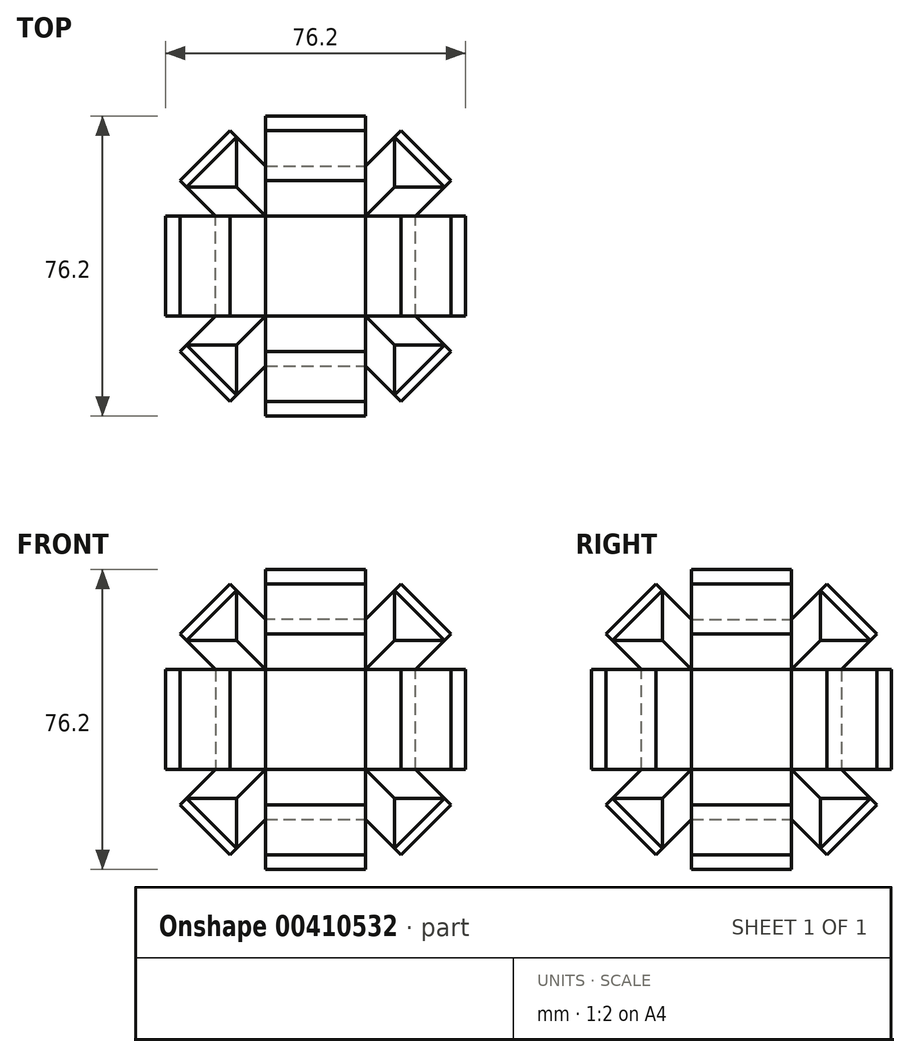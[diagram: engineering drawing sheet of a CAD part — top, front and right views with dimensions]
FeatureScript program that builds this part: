
annotation { "Feature Type Name" : "Feature", "Feature Type Description" : "" }
export const myFeature = defineFeature(function(context is Context, id is Id, definition is map)
    precondition{}
    {
        {
            var Q0;
            Q0=qCreatedBy(makeId("Front.planeOp"),FACE);
            var sketch = newSketch(context, id + "F0", { "sketchPlane" : qUnion([Q0])});
            skLineSegment(sketch, "E0.bottom", {"start": v(-25.4, -25.4) * mm, "end": v(25.4, -25.4) * mm});
            skLineSegment(sketch, "E0.top", {"start": v(-25.4, 25.4) * mm, "end": v(25.4, 25.4) * mm});
            skLineSegment(sketch, "E0.left", {"start": v(-25.4, -25.4) * mm, "end": v(-25.4, 25.4) * mm});
            skLineSegment(sketch, "E0.right", {"start": v(25.4, -25.4) * mm, "end": v(25.4, 25.4) * mm});
            skPoint(sketch, "E0.middle", {"position": v(0, 0) * mm});
            skSolve(sketch);
        }
        {
            var Q0;
            Q0 = qSketchRegion(id + "F0", true);
            extrude(context, id + "F1", {"entities" : qUnion([Q0]), "depth" : 25.4 * mm, "hasSecondDirection" : true, "secondDirectionOppositeDirection" : true, "secondDirectionDepth" : 25.4 * mm});
        }
        {
            var Q0;
            Q0=makeQuery(id+"F1.opExtrude","SWEPT_FACE",FACE,{"disambiguationData":[OSD([sQuery(id+"F0.wireOp",EDGE,"E0.left")])]});
            var Q1;
            Q1=makeQuery(id+"F1.opExtrude","SWEPT_FACE",FACE,{"disambiguationData":[OSD([sQuery(id+"F0.wireOp",EDGE,"E0.bottom")])]});
            var Q2;
            Q2=makeQuery(id+"F1.opExtrude","CAP_FACE",FACE,{"disambiguationData":[OSD([sQuery(id+"F0.wireOp",EDGE,"E0.bottom"),sQuery(id+"F0.wireOp",EDGE,"E0.top"),sQuery(id+"F0.wireOp",EDGE,"E0.left"),sQuery(id+"F0.wireOp",EDGE,"E0.right")])],"isStart":true});
            var Q3;
            Q3=makeQuery(id+"F1.opExtrude","SWEPT_FACE",FACE,{"disambiguationData":[OSD([sQuery(id+"F0.wireOp",EDGE,"E0.right")])]});
            var Q4;
            Q4=makeQuery(id+"F1.opExtrude","SWEPT_FACE",FACE,{"disambiguationData":[OSD([sQuery(id+"F0.wireOp",EDGE,"E0.top")])]});
            var Q5;
            Q5=makeQuery(id+"F1.opExtrude","CAP_FACE",FACE,{"disambiguationData":[OSD([sQuery(id+"F0.wireOp",EDGE,"E0.bottom"),sQuery(id+"F0.wireOp",EDGE,"E0.top"),sQuery(id+"F0.wireOp",EDGE,"E0.left"),sQuery(id+"F0.wireOp",EDGE,"E0.right")])],"isStart":false});
            chamfer(context, id + "F2", {"entities" : qUnion([Q0, Q1, Q2, Q3, Q4, Q5]), "width" : 12.7 * mm, "tangentPropagation" : true});
        }
        {
            var Q0;
            Q0=makeQuery(id+"F1.opExtrude","SWEPT_FACE",FACE,{"disambiguationData":[OSD([sQuery(id+"F0.wireOp",EDGE,"E0.top")])]});
            extrude(context, id + "F3", {"entities" : qUnion([Q0]), "operationType" : NewBodyOperationType.ADD, "depth" : 12.7 * mm});
        }
        {
            var Q0;
            Q0=makeQuery(id+"F1.opExtrude","SWEPT_FACE",FACE,{"disambiguationData":[OSD([sQuery(id+"F0.wireOp",EDGE,"E0.left")])]});
            extrude(context, id + "F4", {"entities" : qUnion([Q0]), "operationType" : NewBodyOperationType.ADD, "depth" : 12.7 * mm});
        }
        {
            var Q0;
            Q0=makeQuery(id+"F1.opExtrude","CAP_FACE",FACE,{"disambiguationData":[OSD([sQuery(id+"F0.wireOp",EDGE,"E0.bottom"),sQuery(id+"F0.wireOp",EDGE,"E0.top"),sQuery(id+"F0.wireOp",EDGE,"E0.left"),sQuery(id+"F0.wireOp",EDGE,"E0.right")])],"isStart":true});
            extrude(context, id + "F5", {"entities" : qUnion([Q0]), "operationType" : NewBodyOperationType.ADD, "depth" : 12.7 * mm});
        }
        {
            var Q0;
            Q0=makeQuery(id+"F1.opExtrude","SWEPT_FACE",FACE,{"disambiguationData":[OSD([sQuery(id+"F0.wireOp",EDGE,"E0.bottom")])]});
            extrude(context, id + "F6", {"entities" : qUnion([Q0]), "operationType" : NewBodyOperationType.ADD, "depth" : 12.7 * mm});
        }
        {
            var Q0;
            Q0=makeQuery(id+"F1.opExtrude","SWEPT_FACE",FACE,{"disambiguationData":[OSD([sQuery(id+"F0.wireOp",EDGE,"E0.right")])]});
            extrude(context, id + "F7", {"entities" : qUnion([Q0]), "operationType" : NewBodyOperationType.ADD, "depth" : 12.7 * mm});
        }
        {
            var Q0;
            Q0=makeQuery(id+"F1.opExtrude","CAP_FACE",FACE,{"disambiguationData":[OSD([sQuery(id+"F0.wireOp",EDGE,"E0.bottom"),sQuery(id+"F0.wireOp",EDGE,"E0.top"),sQuery(id+"F0.wireOp",EDGE,"E0.left"),sQuery(id+"F0.wireOp",EDGE,"E0.right")])],"isStart":false});
            extrude(context, id + "F8", {"entities" : qUnion([Q0]), "operationType" : NewBodyOperationType.ADD, "depth" : 12.7 * mm});
        }
        {
            var Q0;
            {var subQ0=sQuery(id+"F0.wireOp",EDGE,"E0.top");Q0=makeQuery(id+"F2.opChamfer","BLEND_FACE",FACE,{"disambiguationData":[OSD([subQ0]),TDD([makeQuery(id+"F1.opExtrude","CAP_EDGE",EDGE,{"disambiguationData":[OSD([subQ0])],"isStart":true})])]});}
            extrude(context, id + "F9", {"entities" : qUnion([Q0]), "operationType" : NewBodyOperationType.ADD, "depth" : 12.7 * mm});
        }
        {
            var Q0;
            {var subQ0=sQuery(id+"F0.wireOp",EDGE,"E0.right");var subQ1=sQuery(id+"F0.wireOp",EDGE,"E0.top");Q0=makeQuery(id+"F2.opChamfer","BLEND_FACE",FACE,{"disambiguationData":[OSD([subQ1,subQ0]),TDD([makeQuery(id+"F1.opExtrude","SWEPT_EDGE",EDGE,{"disambiguationData":[OSD([subQ1,subQ0])]})])]});}
            extrude(context, id + "F10", {"entities" : qUnion([Q0]), "operationType" : NewBodyOperationType.ADD, "depth" : 12.7 * mm});
        }
        {
            var Q0;
            {var subQ0=sQuery(id+"F0.wireOp",EDGE,"E0.top");Q0=makeQuery(id+"F2.opChamfer","BLEND_FACE",FACE,{"disambiguationData":[OSD([subQ0]),TDD([makeQuery(id+"F1.opExtrude","CAP_EDGE",EDGE,{"disambiguationData":[OSD([subQ0])],"isStart":false})])]});}
            extrude(context, id + "F11", {"entities" : qUnion([Q0]), "operationType" : NewBodyOperationType.ADD, "depth" : 12.7 * mm});
        }
        {
            var Q0;
            {var subQ0=sQuery(id+"F0.wireOp",EDGE,"E0.left");var subQ1=sQuery(id+"F0.wireOp",EDGE,"E0.top");Q0=makeQuery(id+"F2.opChamfer","BLEND_FACE",FACE,{"disambiguationData":[OSD([subQ1,subQ0]),TDD([makeQuery(id+"F1.opExtrude","SWEPT_EDGE",EDGE,{"disambiguationData":[OSD([subQ1,subQ0])]})])]});}
            extrude(context, id + "F12", {"entities" : qUnion([Q0]), "operationType" : NewBodyOperationType.ADD, "depth" : 12.7 * mm});
        }
        {
            var Q0;
            {var subQ0=sQuery(id+"F0.wireOp",EDGE,"E0.bottom");Q0=makeQuery(id+"F2.opChamfer","BLEND_FACE",FACE,{"disambiguationData":[OSD([subQ0]),TDD([makeQuery(id+"F1.opExtrude","CAP_EDGE",EDGE,{"disambiguationData":[OSD([subQ0])],"isStart":true})])]});}
            extrude(context, id + "F13", {"entities" : qUnion([Q0]), "operationType" : NewBodyOperationType.ADD, "depth" : 12.7 * mm});
        }
        {
            var Q0;
            {var subQ0=sQuery(id+"F0.wireOp",EDGE,"E0.left");var subQ1=sQuery(id+"F0.wireOp",EDGE,"E0.bottom");Q0=makeQuery(id+"F2.opChamfer","BLEND_FACE",FACE,{"disambiguationData":[OSD([subQ1,subQ0]),TDD([makeQuery(id+"F1.opExtrude","SWEPT_EDGE",EDGE,{"disambiguationData":[OSD([subQ1,subQ0])]})])]});}
            extrude(context, id + "F14", {"entities" : qUnion([Q0]), "operationType" : NewBodyOperationType.ADD, "depth" : 12.7 * mm});
        }
        {
            var Q0;
            {var subQ0=sQuery(id+"F0.wireOp",EDGE,"E0.bottom");Q0=makeQuery(id+"F2.opChamfer","BLEND_FACE",FACE,{"disambiguationData":[OSD([subQ0]),TDD([makeQuery(id+"F1.opExtrude","CAP_EDGE",EDGE,{"disambiguationData":[OSD([subQ0])],"isStart":false})])]});}
            extrude(context, id + "F15", {"entities" : qUnion([Q0]), "operationType" : NewBodyOperationType.ADD, "depth" : 12.7 * mm});
        }
        {
            var Q0;
            {var subQ0=sQuery(id+"F0.wireOp",EDGE,"E0.left");Q0=makeQuery(id+"F2.opChamfer","BLEND_FACE",FACE,{"disambiguationData":[OSD([subQ0]),TDD([makeQuery(id+"F1.opExtrude","CAP_EDGE",EDGE,{"disambiguationData":[OSD([subQ0])],"isStart":false})])]});}
            extrude(context, id + "F16", {"entities" : qUnion([Q0]), "operationType" : NewBodyOperationType.ADD, "depth" : 12.7 * mm});
        }
        {
            var Q0;
            {var subQ0=sQuery(id+"F0.wireOp",EDGE,"E0.left");Q0=makeQuery(id+"F2.opChamfer","BLEND_FACE",FACE,{"disambiguationData":[OSD([subQ0]),TDD([makeQuery(id+"F1.opExtrude","CAP_EDGE",EDGE,{"disambiguationData":[OSD([subQ0])],"isStart":true})])]});}
            extrude(context, id + "F17", {"entities" : qUnion([Q0]), "operationType" : NewBodyOperationType.ADD, "depth" : 12.7 * mm});
        }
        {
            var Q0;
            {var subQ0=sQuery(id+"F0.wireOp",EDGE,"E0.right");Q0=makeQuery(id+"F2.opChamfer","BLEND_FACE",FACE,{"disambiguationData":[OSD([subQ0]),TDD([makeQuery(id+"F1.opExtrude","CAP_EDGE",EDGE,{"disambiguationData":[OSD([subQ0])],"isStart":true})])]});}
            extrude(context, id + "F18", {"entities" : qUnion([Q0]), "operationType" : NewBodyOperationType.ADD, "depth" : 12.7 * mm});
        }
        {
            var Q0;
            {var subQ0=sQuery(id+"F0.wireOp",EDGE,"E0.right");Q0=makeQuery(id+"F2.opChamfer","BLEND_FACE",FACE,{"disambiguationData":[OSD([subQ0]),TDD([makeQuery(id+"F1.opExtrude","CAP_EDGE",EDGE,{"disambiguationData":[OSD([subQ0])],"isStart":false})])]});}
            extrude(context, id + "F19", {"entities" : qUnion([Q0]), "operationType" : NewBodyOperationType.ADD, "depth" : 12.7 * mm});
        }
        {
            var Q0;
            {var subQ0=sQuery(id+"F0.wireOp",EDGE,"E0.right");var subQ1=sQuery(id+"F0.wireOp",EDGE,"E0.bottom");Q0=makeQuery(id+"F2.opChamfer","BLEND_FACE",FACE,{"disambiguationData":[OSD([subQ1,subQ0]),TDD([makeQuery(id+"F1.opExtrude","SWEPT_EDGE",EDGE,{"disambiguationData":[OSD([subQ1,subQ0])]})])]});}
            extrude(context, id + "F20", {"entities" : qUnion([Q0]), "operationType" : NewBodyOperationType.ADD, "depth" : 12.7 * mm});
        }
        {
            var Q0;
            {var subQ0=sQuery(id+"F0.wireOp",EDGE,"E0.right");var subQ1=sQuery(id+"F0.wireOp",EDGE,"E0.top");Q0=makeQuery(id+"F2.opChamfer","BLEND_FACE",FACE,{"disambiguationData":[OSD([subQ1,subQ0]),TDD([makeQuery(id+"F1.opExtrude","CAP_VERTEX",VERTEX,{"disambiguationData":[OSD([subQ1,subQ0])],"isStart":false})])]});}
            var sketch = newSketch(context, id + "F21", { "sketchPlane" : qUnion([Q0])});
            skSolve(sketch);
        }
        {
            var Q0;
            {var subQ0=sQuery(id+"F0.wireOp",EDGE,"E0.right");var subQ1=sQuery(id+"F0.wireOp",EDGE,"E0.top");var subQ2=makeQuery(id+"F1.opExtrude","CAP_VERTEX",VERTEX,{"disambiguationData":[OSD([subQ1,subQ0])],"isStart":false});Q0=makeQuery(id+"F21.imprint","IMPRINT",FACE,{"disambiguationData":[TD([[makeQuery(id+"F21.imprint","IMPRINT",EDGE,{"derivedFrom":makeQuery(id+"F11.boolean.opBoolean","MERGE",EDGE,{"derivedFrom":[makeQuery(id+"F2.opChamfer","BLEND_EDGE",EDGE,{"blendedFrom":[subQ2,makeQuery(id+"F1.opExtrude","CAP_EDGE",EDGE,{"disambiguationData":[OSD([subQ1])],"isStart":false})],"blendedInto":[]}),makeQuery(id+"F11.opExtrude","CAP_EDGE",EDGE,{"disambiguationData":[OSD([subQ1,subQ0])],"isStart":true})]})}),-1.0]])]});}
            extrude(context, id + "F22", {"entities" : qUnion([Q0]), "operationType" : NewBodyOperationType.ADD, "depth" : 12.7 * mm});
        }
        {
            var Q0;
            {var subQ0=sQuery(id+"F0.wireOp",EDGE,"E0.right");var subQ1=sQuery(id+"F0.wireOp",EDGE,"E0.top");Q0=makeQuery(id+"F2.opChamfer","BLEND_FACE",FACE,{"disambiguationData":[OSD([subQ1,subQ0]),TDD([makeQuery(id+"F1.opExtrude","CAP_VERTEX",VERTEX,{"disambiguationData":[OSD([subQ1,subQ0])],"isStart":true})])]});}
            extrude(context, id + "F23", {"entities" : qUnion([Q0]), "operationType" : NewBodyOperationType.ADD, "depth" : 12.7 * mm});
        }
        {
            var Q0;
            {var subQ0=sQuery(id+"F0.wireOp",EDGE,"E0.left");var subQ1=sQuery(id+"F0.wireOp",EDGE,"E0.top");Q0=makeQuery(id+"F2.opChamfer","BLEND_FACE",FACE,{"disambiguationData":[OSD([subQ1,subQ0]),TDD([makeQuery(id+"F1.opExtrude","CAP_VERTEX",VERTEX,{"disambiguationData":[OSD([subQ1,subQ0])],"isStart":true})])]});}
            extrude(context, id + "F24", {"entities" : qUnion([Q0]), "operationType" : NewBodyOperationType.ADD, "depth" : 12.7 * mm});
        }
        {
            var Q0;
            {var subQ0=sQuery(id+"F0.wireOp",EDGE,"E0.left");var subQ1=sQuery(id+"F0.wireOp",EDGE,"E0.top");Q0=makeQuery(id+"F2.opChamfer","BLEND_FACE",FACE,{"disambiguationData":[OSD([subQ1,subQ0]),TDD([makeQuery(id+"F1.opExtrude","CAP_VERTEX",VERTEX,{"disambiguationData":[OSD([subQ1,subQ0])],"isStart":false})])]});}
            extrude(context, id + "F25", {"entities" : qUnion([Q0]), "operationType" : NewBodyOperationType.ADD, "depth" : 12.7 * mm});
        }
        {
            var Q0;
            {var subQ0=sQuery(id+"F0.wireOp",EDGE,"E0.left");var subQ1=sQuery(id+"F0.wireOp",EDGE,"E0.bottom");Q0=makeQuery(id+"F2.opChamfer","BLEND_FACE",FACE,{"disambiguationData":[OSD([subQ1,subQ0]),TDD([makeQuery(id+"F1.opExtrude","CAP_VERTEX",VERTEX,{"disambiguationData":[OSD([subQ1,subQ0])],"isStart":false})])]});}
            extrude(context, id + "F26", {"entities" : qUnion([Q0]), "operationType" : NewBodyOperationType.ADD, "depth" : 12.7 * mm});
        }
        {
            var Q0;
            {var subQ0=sQuery(id+"F0.wireOp",EDGE,"E0.left");var subQ1=sQuery(id+"F0.wireOp",EDGE,"E0.bottom");Q0=makeQuery(id+"F2.opChamfer","BLEND_FACE",FACE,{"disambiguationData":[OSD([subQ1,subQ0]),TDD([makeQuery(id+"F1.opExtrude","CAP_VERTEX",VERTEX,{"disambiguationData":[OSD([subQ1,subQ0])],"isStart":true})])]});}
            extrude(context, id + "F27", {"entities" : qUnion([Q0]), "operationType" : NewBodyOperationType.ADD, "depth" : 12.7 * mm});
        }
        {
            var Q0;
            {var subQ0=sQuery(id+"F0.wireOp",EDGE,"E0.right");var subQ1=sQuery(id+"F0.wireOp",EDGE,"E0.bottom");Q0=makeQuery(id+"F2.opChamfer","BLEND_FACE",FACE,{"disambiguationData":[OSD([subQ1,subQ0]),TDD([makeQuery(id+"F1.opExtrude","CAP_VERTEX",VERTEX,{"disambiguationData":[OSD([subQ1,subQ0])],"isStart":true})])]});}
            extrude(context, id + "F28", {"entities" : qUnion([Q0]), "operationType" : NewBodyOperationType.ADD, "depth" : 12.7 * mm});
        }
        {
            var Q0;
            {var subQ0=sQuery(id+"F0.wireOp",EDGE,"E0.right");var subQ1=sQuery(id+"F0.wireOp",EDGE,"E0.bottom");Q0=makeQuery(id+"F2.opChamfer","BLEND_FACE",FACE,{"disambiguationData":[OSD([subQ1,subQ0]),TDD([makeQuery(id+"F1.opExtrude","CAP_VERTEX",VERTEX,{"disambiguationData":[OSD([subQ1,subQ0])],"isStart":false})])]});}
            extrude(context, id + "F29", {"entities" : qUnion([Q0]), "operationType" : NewBodyOperationType.ADD, "depth" : 12.7 * mm});
        }
    });
